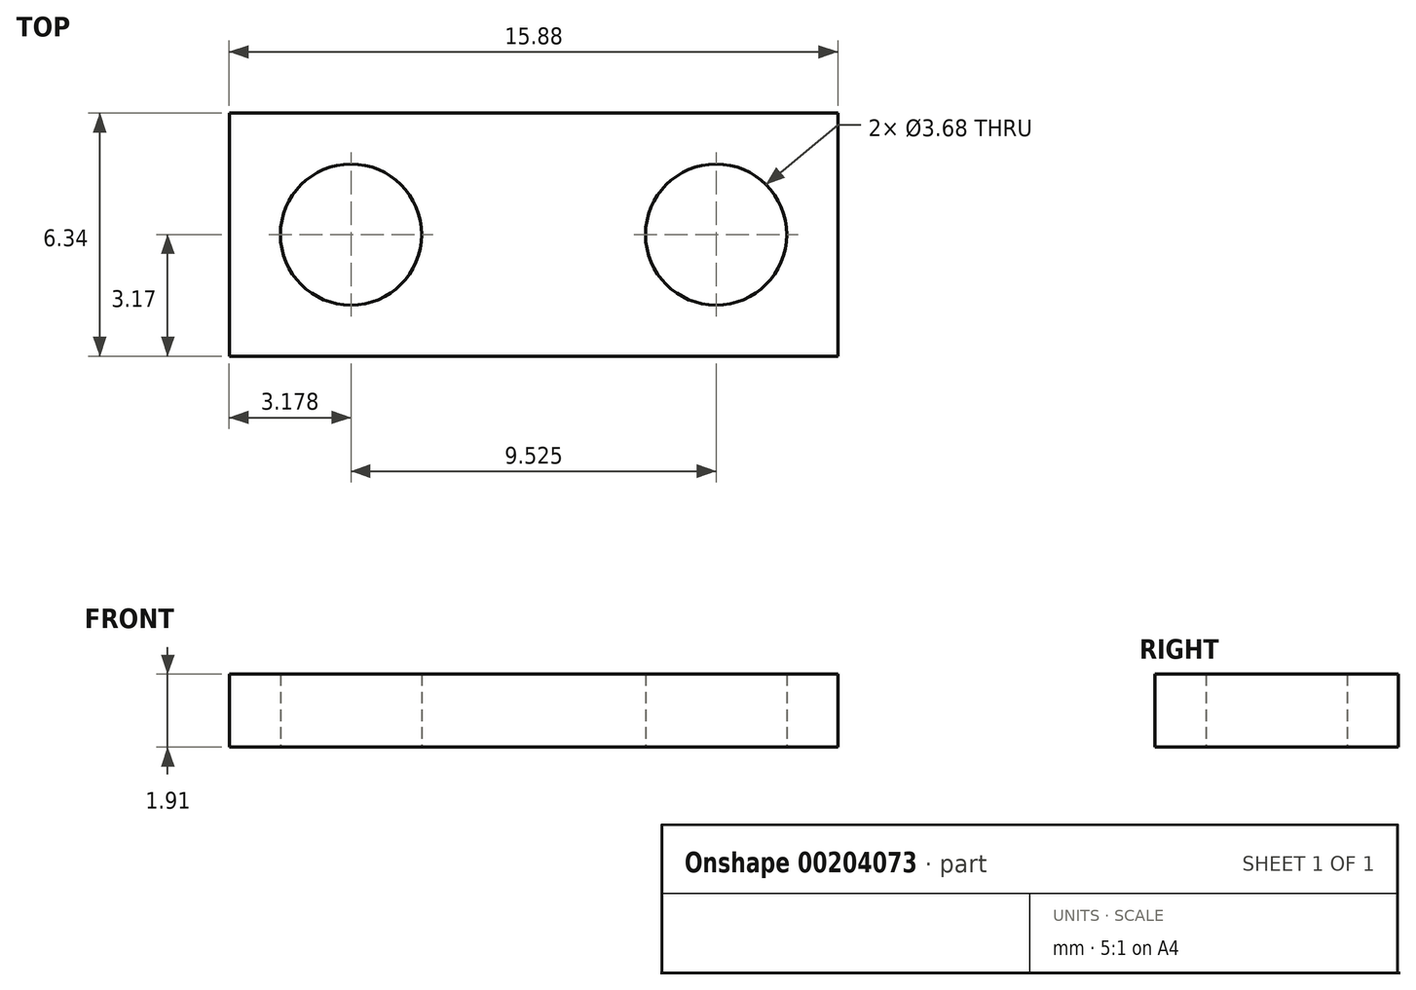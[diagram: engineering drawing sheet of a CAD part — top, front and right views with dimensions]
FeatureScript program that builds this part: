
annotation { "Feature Type Name" : "Feature", "Feature Type Description" : "" }
export const myFeature = defineFeature(function(context is Context, id is Id, definition is map)
    precondition{}
    {
        {
            var Q0;
            Q0=qCreatedBy(makeId("Top.planeOp"),FACE);
            var sketch = newSketch(context, id + "F0", { "sketchPlane" : qUnion([Q0])});
            skLineSegment(sketch, "E0", {"start": v(0, 0) * mm, "end": v(7.94, 0) * mm, "construction": true});
            skLineSegment(sketch, "E1", {"start": v(7.94, 3.18) * mm, "end": v(7.94, -3.17) * mm});
            skLineSegment(sketch, "E2", {"start": v(7.94, -3.17) * mm, "end": v(-7.94, -3.18) * mm});
            skLineSegment(sketch, "E3", {"start": v(-7.94, -3.17) * mm, "end": v(-7.94, 3.17) * mm});
            skLineSegment(sketch, "E4", {"start": v(-7.94, 3.17) * mm, "end": v(7.94, 3.18) * mm});
            skLineSegment(sketch, "E5", {"start": v(0, 0) * mm, "end": v(-7.94, 0) * mm, "construction": true});
            skLineSegment(sketch, "E6", {"start": v(-7.94, 0) * mm, "end": v(-4.76, 0) * mm, "construction": true});
            skLineSegment(sketch, "E7", {"start": v(7.94, 0) * mm, "end": v(4.76, 0) * mm, "construction": true});
            skCircle(sketch, "E8", {"center": v(-4.76, 0) * mm, "radius": 1.84 * mm});
            skCircle(sketch, "E9", {"center": v(4.76, 0) * mm, "radius": 1.84 * mm});
            skSolve(sketch);
        }
        {
            var Q0;
            Q0 = qSketchRegion(id + "F0", true);
            extrude(context, id + "F1", {"entities" : qUnion([Q0]), "depth" : 1.9 * mm});
        }
    });
